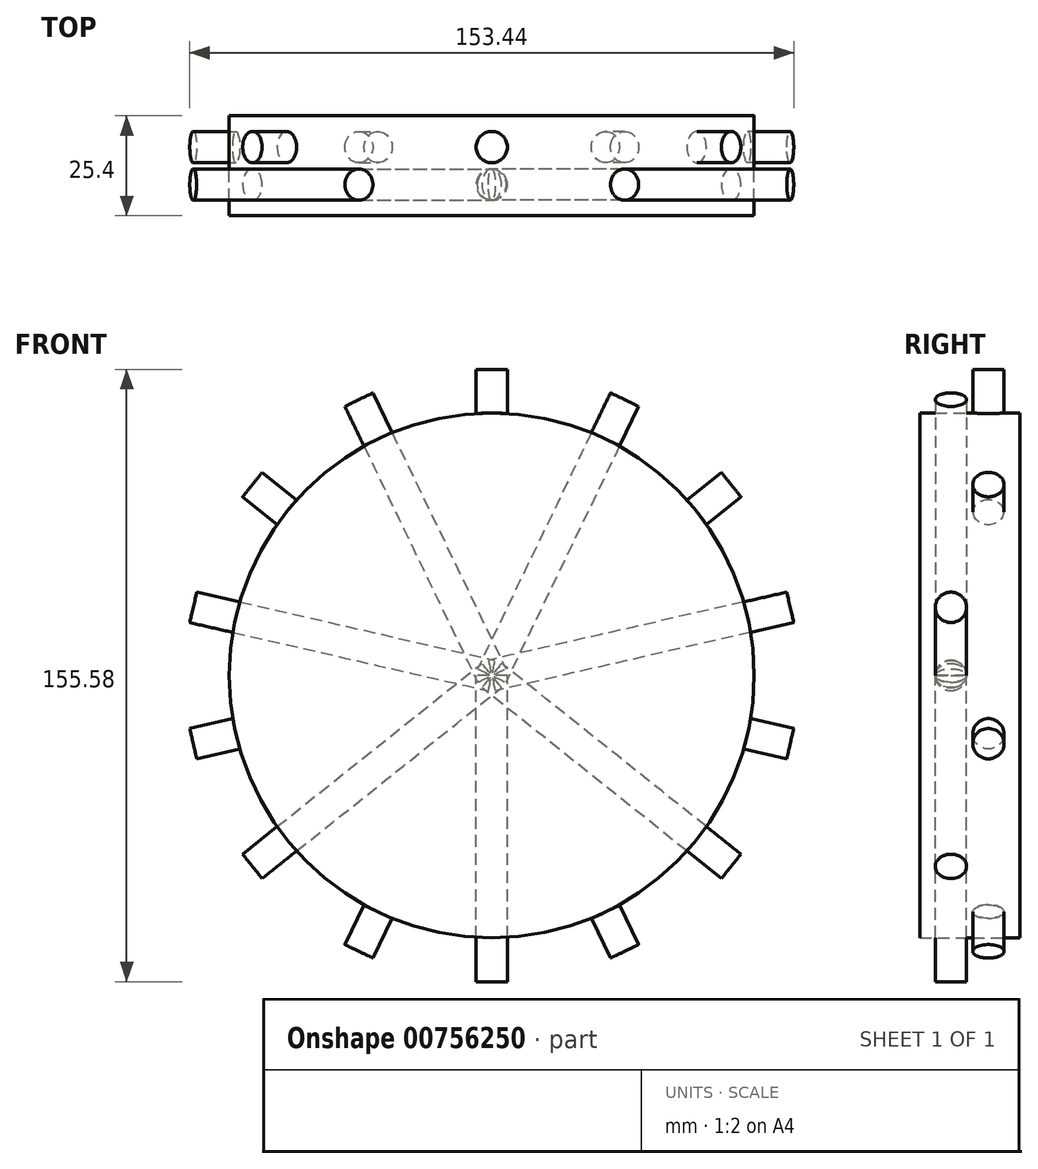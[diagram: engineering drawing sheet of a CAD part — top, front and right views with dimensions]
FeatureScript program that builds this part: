
annotation { "Feature Type Name" : "Feature", "Feature Type Description" : "" }
export const myFeature = defineFeature(function(context is Context, id is Id, definition is map)
    precondition{}
    {
        {
            var Q0;
            Q0=qCreatedBy(makeId("Front.planeOp"),FACE);
            var sketch = newSketch(context, id + "F0", { "sketchPlane" : qUnion([Q0])});
            skCircle(sketch, "E0", {"center": v(0, 0) * mm, "radius": 66.68 * mm});
            skSolve(sketch);
        }
        {
            var Q0;
            Q0 = qSketchRegion(id + "F0", true);
            extrude(context, id + "F1", {"entities" : qUnion([Q0]), "depth" : 25.4 * mm, "offsetDistance" : 25.4 * mm});
        }
        {
            var Q0;
            Q0=qCreatedBy(makeId("Top.planeOp"),FACE);
            var sketch = newSketch(context, id + "F2", { "sketchPlane" : qUnion([Q0])});
            skCircle(sketch, "E1", {"center": v(0, -7.94) * mm, "radius": 3.97 * mm});
            skSolve(sketch);
        }
        {
            var Q0;
            Q0 = qSketchRegion(id + "F2", true);
            extrude(context, id + "F3", {"entities" : qUnion([Q0]), "operationType" : NewBodyOperationType.ADD, "depth" : 77.8 * mm, "offsetDistance" : 25.4 * mm});
        }
        {
            var Q0;
            Q0=qCreatedBy(makeId("Top.planeOp"),FACE);
            var sketch = newSketch(context, id + "F4", { "sketchPlane" : qUnion([Q0])});
            skCircle(sketch, "E2", {"center": v(0, -17.46) * mm, "radius": 3.97 * mm});
            skSolve(sketch);
        }
        {
            var Q0;
            Q0=makeQuery(id+"F1.opExtrude","SWEPT_BODY",BODY,{"disambiguationData":[OSD([sQuery(id+"F0.wireOp",EDGE,"E0")])]});
            var Q1;
            Q1=makeQuery(id+"F1.opExtrude","CAP_EDGE",EDGE,{"disambiguationData":[OSD([sQuery(id+"F0.wireOp",EDGE,"E0")])],"isStart":true});
            circularPattern(context, id + "F5", {"entities" : qUnion([Q0]), "axis" : qUnion([Q1]), "angle" : 360 * degree, "instanceCount" : 7, "equalSpace" : true});
        }
        {
            var Q0;
            Q0=makeQuery(id+"F4.imprint","IMPRINT",FACE,{"disambiguationData":[TD([[makeQuery(id+"F4.imprint","IMPRINT",EDGE,{"derivedFrom":sQuery(id+"F4.wireOp",EDGE,"E2")}),1.0]])]});
            extrude(context, id + "F6", {"entities" : qUnion([Q0]), "oppositeDirection" : true, "depth" : 77.8 * mm, "offsetDistance" : 25.4 * mm});
        }
        {
            var Q0;
            Q0=makeQuery(id+"F6.opExtrude","SWEPT_BODY",BODY,{"disambiguationData":[OSD([sQuery(id+"F4.wireOp",EDGE,"E2")])]});
            var Q1;
            Q1=makeQuery(id+"F1.opExtrude","SWEPT_BODY",BODY,{"disambiguationData":[OSD([sQuery(id+"F0.wireOp",EDGE,"E0")])]});
            var Q2;
            Q2=makeQuery(id+"F1.opExtrude","CAP_EDGE",EDGE,{"disambiguationData":[OSD([sQuery(id+"F0.wireOp",EDGE,"E0")])],"isStart":false});
            circularPattern(context, id + "F7", {"entities" : qUnion([Q0, Q1]), "axis" : qUnion([Q2]), "angle" : 360 * degree, "instanceCount" : 7, "equalSpace" : true});
        }
    });
